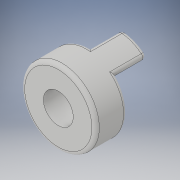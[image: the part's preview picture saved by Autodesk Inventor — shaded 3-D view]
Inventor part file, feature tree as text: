
AUTODESK INVENTOR PART (.ipt)
format: ipt  version: 2018 (Build 220112000, 112)  size: 209,920 bytes
history: native  units: in
note: dims shown in document units (in); Inventor stores cm internally (conversion verified against a paired STEP export)
features: extrude x2, fillet x2, sketch x1, pattern_circular x1
ambient origin geometry x8: Origin, YZ Plane, XZ Plane, XY Plane, X Axis, Y Axis, Z Axis, Center Point
bodies: Solid1 (feature_tree)
feature tree (6):
  sketch  "Sketch1"  dims[d0=0.625in d1=0.25in d2=45.0deg d3=0.05in d4=0.2656in d5=0.0in d6=0.2656in d7=0.0in d8=0.0312in d9=0.7874in d10=360.0deg d12=0.0312in]
  extrude  "Extrusion1"  Depth=0.0312in
  extrude  "Extrusion2"  TaperAngle=45.0deg  [1 undecoded]
  fillet  "Fillet1"  Radius=0.05in
  pattern_circular  "Circular Pattern1"  [2 undecoded]
  fillet  "Fillet2"  Radius=0.2656in
note: 3 required parameter values undecoded (feature->parameter linkage not recoverable at this tier; creation-order binding heuristic only, values carry confidence <= 0.55)
